annotation { "Feature Type Name" : "Feature", "Feature Type Description" : "" }
export const myFeature = defineFeature(function(context is Context, id is Id, definition is map)
    precondition{}
    {
        {
            var Q0;
            Q0=qCreatedBy(makeId("Right.planeOp"),FACE);
            var sketch = newSketch(context, id + "F0", { "sketchPlane" : qUnion([Q0])});
            skLineSegment(sketch, "E0.bottom", {"start": v(-68.65, 40) * mm, "end": v(-51.35, 40) * mm});
            skLineSegment(sketch, "E0.top", {"start": v(-68.65, -20) * mm, "end": v(68.65, -20) * mm});
            skLineSegment(sketch, "E0.left", {"start": v(-75, 33.65) * mm, "end": v(-75, -13.65) * mm});
            skLineSegment(sketch, "E0.right", {"start": v(75, 33.65) * mm, "end": v(75, -13.65) * mm});
            skLineSegment(sketch, "E1.top", {"start": v(-38.65, 80) * mm, "end": v(43.65, 80) * mm});
            skLineSegment(sketch, "E1.left", {"start": v(-45, 46.35) * mm, "end": v(-45, 73.65) * mm});
            skLineSegment(sketch, "E1.right", {"start": v(50, 46.35) * mm, "end": v(50, 73.65) * mm});
            skArc(sketch, "E2.filletArc", {"start": v(-51.35, 40) * mm, "mid": v(-46.86, 41.86) * mm, "end": v(-45, 46.35) * mm});
            skLineSegment(sketch, "E3", {"start": v(56.35, 40) * mm, "end": v(68.65, 40) * mm});
            skPoint(sketch, "E4.visualSharp", {"position": v(50, 40) * mm});
            skArc(sketch, "E4.filletArc", {"start": v(50, 46.35) * mm, "mid": v(51.86, 41.86) * mm, "end": v(56.35, 40) * mm});
            skPoint(sketch, "E5.visualSharp", {"position": v(50, 80) * mm});
            skArc(sketch, "E5.filletArc", {"start": v(50, 73.65) * mm, "mid": v(48.14, 78.14) * mm, "end": v(43.65, 80) * mm});
            skPoint(sketch, "E6.visualSharp", {"position": v(-45, 80) * mm});
            skArc(sketch, "E6.filletArc", {"start": v(-38.65, 80) * mm, "mid": v(-43.14, 78.14) * mm, "end": v(-45, 73.65) * mm});
            skPoint(sketch, "E7.visualSharp", {"position": v(-75, 40) * mm});
            skArc(sketch, "E7.filletArc", {"start": v(-68.65, 40) * mm, "mid": v(-73.14, 38.14) * mm, "end": v(-75, 33.65) * mm});
            skPoint(sketch, "E8.visualSharp", {"position": v(75, 40) * mm});
            skArc(sketch, "E8.filletArc", {"start": v(75, 33.65) * mm, "mid": v(73.14, 38.14) * mm, "end": v(68.65, 40) * mm});
            skPoint(sketch, "E9.visualSharp", {"position": v(-75, -20) * mm});
            skArc(sketch, "E9.filletArc", {"start": v(-75, -13.65) * mm, "mid": v(-73.14, -18.14) * mm, "end": v(-68.65, -20) * mm});
            skPoint(sketch, "E10.visualSharp", {"position": v(75, -20) * mm});
            skArc(sketch, "E10.filletArc", {"start": v(68.65, -20) * mm, "mid": v(73.14, -18.14) * mm, "end": v(75, -13.65) * mm});
            skSolve(sketch);
        }
        {
            var Q0;
            Q0 = qSketchRegion(id + "F0", true);
            extrude(context, id + "F1", {"entities" : qUnion([Q0]), "endBound" : BoundingType.SYMMETRIC, "depth" : 100 * mm});
        }
        {
            var Q0;
            Q0=makeQuery(id+"F1.opExtrude","SWEPT_FACE",FACE,{"disambiguationData":[OSD([sQuery(id+"F0.wireOp",EDGE,"E1.top")])]});
            var sketch = newSketch(context, id + "F2", { "sketchPlane" : qUnion([Q0])});
            skLineSegment(sketch, "E11.bottom", {"start": v(-45, 40) * mm, "end": v(45, 40) * mm});
            skLineSegment(sketch, "E11.top", {"start": v(-45, -35) * mm, "end": v(45, -35) * mm});
            skLineSegment(sketch, "E11.left", {"start": v(-45, 40) * mm, "end": v(-45, -35) * mm});
            skLineSegment(sketch, "E11.right", {"start": v(45, 40) * mm, "end": v(45, -35) * mm});
            skSolve(sketch);
        }
        {
            var Q0;
            Q0=makeQuery(id+"F2.imprint","IMPRINT",FACE,{"disambiguationData":[TD([[makeQuery(id+"F2.imprint","IMPRINT",EDGE,{"derivedFrom":sQuery(id+"F2.wireOp",EDGE,"E11.bottom")}),-1.0]])]});
            extrude(context, id + "F3", {"entities" : qUnion([Q0]), "operationType" : NewBodyOperationType.REMOVE, "oppositeDirection" : true, "depth" : 95 * mm});
        }
        {
            var Q0;
            Q0=makeQuery(id+"F1.opExtrude","SWEPT_FACE",FACE,{"disambiguationData":[OSD([sQuery(id+"F0.wireOp",EDGE,"E0.bottom")])]});
            var sketch = newSketch(context, id + "F4", { "sketchPlane" : qUnion([Q0])});
            skLineSegment(sketch, "E12.bottom", {"start": v(-48, -54.65) * mm, "end": v(-2, -54.65) * mm});
            skLineSegment(sketch, "E12.top", {"start": v(-48, -66.65) * mm, "end": v(-2, -66.65) * mm});
            skLineSegment(sketch, "E12.left", {"start": v(-48, -54.65) * mm, "end": v(-48, -66.65) * mm});
            skLineSegment(sketch, "E12.right", {"start": v(-2, -54.65) * mm, "end": v(-2, -66.65) * mm});
            skLineSegment(sketch, "E13.bottom", {"start": v(2, -54.65) * mm, "end": v(48, -54.65) * mm});
            skLineSegment(sketch, "E13.top", {"start": v(2, -66.65) * mm, "end": v(48, -66.65) * mm});
            skLineSegment(sketch, "E13.left", {"start": v(2, -54.65) * mm, "end": v(2, -66.65) * mm});
            skLineSegment(sketch, "E13.right", {"start": v(48, -54.65) * mm, "end": v(48, -66.65) * mm});
            skSolve(sketch);
        }
        {
            var Q0;
            Q0 = qSketchRegion(id + "F4", true);
            extrude(context, id + "F5", {"entities" : qUnion([Q0]), "operationType" : NewBodyOperationType.REMOVE, "oppositeDirection" : true, "depth" : 55 * mm});
        }
        {
            var Q0;
            Q0=makeQuery(id+"F1.opExtrude","SWEPT_FACE",FACE,{"disambiguationData":[OSD([sQuery(id+"F0.wireOp",EDGE,"E3")])]});
            var sketch = newSketch(context, id + "F6", { "sketchPlane" : qUnion([Q0])});
            skLineSegment(sketch, "E14.bottom", {"start": v(-48, 67.65) * mm, "end": v(48, 67.65) * mm});
            skLineSegment(sketch, "E14.top", {"start": v(-48, 57.35) * mm, "end": v(48, 57.35) * mm});
            skLineSegment(sketch, "E14.left", {"start": v(-48, 67.65) * mm, "end": v(-48, 57.35) * mm});
            skLineSegment(sketch, "E14.right", {"start": v(48, 67.65) * mm, "end": v(48, 57.35) * mm});
            skSolve(sketch);
        }
        {
            var Q0;
            Q0=makeQuery(id+"F6.imprint","IMPRINT",FACE,{"disambiguationData":[TD([[makeQuery(id+"F6.imprint","IMPRINT",EDGE,{"derivedFrom":sQuery(id+"F6.wireOp",EDGE,"E14.bottom")}),-1.0]])]});
            extrude(context, id + "F7", {"entities" : qUnion([Q0]), "operationType" : NewBodyOperationType.REMOVE, "oppositeDirection" : true, "depth" : 55 * mm});
        }
        {
            var Q0;
            Q0=makeQuery(id+"F1.opExtrude","CAP_FACE",FACE,{"disambiguationData":[OSD([sQuery(id+"F0.wireOp",EDGE,"E0.bottom"),sQuery(id+"F0.wireOp",EDGE,"E0.top"),sQuery(id+"F0.wireOp",EDGE,"E0.left"),sQuery(id+"F0.wireOp",EDGE,"E0.right"),sQuery(id+"F0.wireOp",EDGE,"E1.top"),sQuery(id+"F0.wireOp",EDGE,"E1.left"),sQuery(id+"F0.wireOp",EDGE,"E1.right"),sQuery(id+"F0.wireOp",EDGE,"E2.filletArc"),sQuery(id+"F0.wireOp",EDGE,"E3"),sQuery(id+"F0.wireOp",EDGE,"E4.filletArc"),sQuery(id+"F0.wireOp",EDGE,"E5.filletArc"),sQuery(id+"F0.wireOp",EDGE,"E6.filletArc"),sQuery(id+"F0.wireOp",EDGE,"E7.filletArc"),sQuery(id+"F0.wireOp",EDGE,"E8.filletArc"),sQuery(id+"F0.wireOp",EDGE,"E9.filletArc"),sQuery(id+"F0.wireOp",EDGE,"E10.filletArc")])],"isStart":false});
            var sketch = newSketch(context, id + "F8", { "sketchPlane" : qUnion([Q0])});
            skText(sketch, "E15", { "text": "Pioneer", "fontName": "OpenSans-Regular.ttf"});
            skText(sketch, "E16", { "text": "Secondary School", "fontName": "OpenSans-Regular.ttf"});
            skText(sketch, "E17", { "text": "Applied Learning", "fontName": "OpenSans-Regular.ttf"});
            skText(sketch, "E18", { "text": "Programme", "fontName": "OpenSans-Regular.ttf"});
            const initialGuessF8  = {"E15": [-0.02612, 0.04144, 1, 0, 0.01], "E16": [-0.05522, 0.02405, 1, 0, 0.01], "E17": [-0.05386, 0.00482, 1, 0, 0.01], "E18": [-0.03771, -0.01, 1, 0, 0.01]};
            skSetInitialGuess(sketch, initialGuessF8);
            skSolve(sketch);
        }
        {
            var Q0;
            Q0 = qSketchRegion(id + "F8", true);
            extrude(context, id + "F9", {"entities" : qUnion([Q0]), "operationType" : NewBodyOperationType.REMOVE, "oppositeDirection" : true, "depth" : 25 * mm});
        }
        {
            var Q0;
            Q0=qCreatedBy(makeId("Right.planeOp"),FACE);
            var sketch = newSketch(context, id + "F10", { "sketchPlane" : qUnion([Q0])});
            skArc(sketch, "E19", {"start": v(-63.79, -20.22) * mm, "mid": v(-54.13, -29.71) * mm, "end": v(-44.47, -20.22) * mm});
            skArc(sketch, "E20", {"start": v(64.85, -20.22) * mm, "mid": v(54.15, -30.73) * mm, "end": v(43.5, -20.18) * mm});
            skLineSegment(sketch, "E21", {"start": v(-63.79, -20.22) * mm, "end": v(-44.47, -20.22) * mm});
            skLineSegment(sketch, "E22", {"start": v(43.5, -20.18) * mm, "end": v(64.85, -20.22) * mm});
            skSolve(sketch);
        }
        {
            var Q0;
            Q0 = qSketchRegion(id + "F10", true);
            extrude(context, id + "F11", {"entities" : qUnion([Q0]), "endBound" : BoundingType.SYMMETRIC, "depth" : 100 * mm});
        }
        {
            var Q0;
            Q0=makeQuery(id+"F1.opExtrude","SWEPT_FACE",FACE,{"disambiguationData":[OSD([sQuery(id+"F0.wireOp",EDGE,"E1.left")])]});
            var sketch = newSketch(context, id + "F12", { "sketchPlane" : qUnion([Q0])});
            skLineSegment(sketch, "E23.bottom", {"start": v(-46.74, 70.76) * mm, "end": v(46.17, 70.76) * mm});
            skLineSegment(sketch, "E23.top", {"start": v(-46.74, 49.39) * mm, "end": v(46.17, 49.39) * mm});
            skLineSegment(sketch, "E23.left", {"start": v(-46.74, 70.76) * mm, "end": v(-46.74, 49.39) * mm});
            skLineSegment(sketch, "E23.right", {"start": v(46.17, 70.76) * mm, "end": v(46.17, 49.39) * mm});
            skSolve(sketch);
        }
        {
            var Q0;
            Q0=makeQuery(id+"F12.imprint","IMPRINT",FACE,{"disambiguationData":[TD([[makeQuery(id+"F12.imprint","IMPRINT",EDGE,{"derivedFrom":sQuery(id+"F12.wireOp",EDGE,"E23.bottom")}),-1.0]])]});
            extrude(context, id + "F13", {"entities" : qUnion([Q0]), "operationType" : NewBodyOperationType.REMOVE, "oppositeDirection" : true, "depth" : 1 * mm});
        }
    });